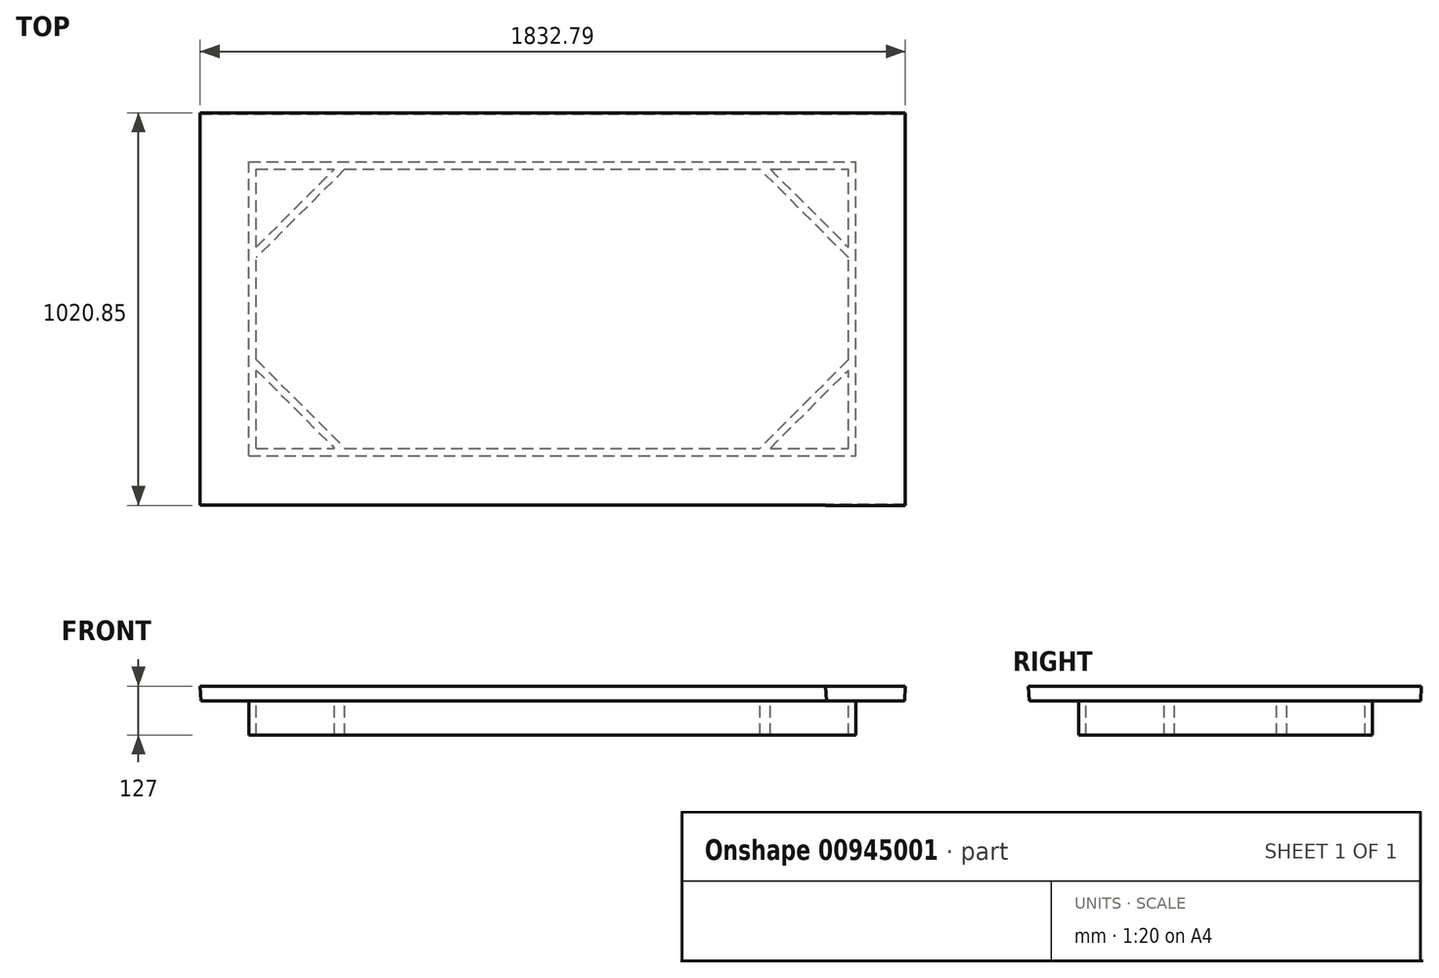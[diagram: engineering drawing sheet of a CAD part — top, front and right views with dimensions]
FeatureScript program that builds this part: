
annotation { "Feature Type Name" : "Feature", "Feature Type Description" : "" }
export const myFeature = defineFeature(function(context is Context, id is Id, definition is map)
    precondition{}
    {
        {
            var Q0;
            Q0=qCreatedBy(makeId("Top.planeOp"),FACE);
            var sketch = newSketch(context, id + "F0", { "sketchPlane" : qUnion([Q0])});
            skLineSegment(sketch, "E0.bottom", {"start": v(-617.33, 1070.93) * mm, "end": v(805.07, 1070.93) * mm});
            skLineSegment(sketch, "E0.top", {"start": v(-617.33, 867.73) * mm, "end": v(805.07, 867.73) * mm});
            skLineSegment(sketch, "E0.left", {"start": v(-617.33, 1070.93) * mm, "end": v(-617.33, 867.73) * mm});
            skLineSegment(sketch, "E0.right", {"start": v(805.07, 1070.93) * mm, "end": v(805.07, 867.73) * mm});
            skLineSegment(sketch, "E1.top", {"start": v(-617.33, 664.53) * mm, "end": v(805.07, 664.53) * mm});
            skLineSegment(sketch, "E1.left", {"start": v(-617.33, 867.73) * mm, "end": v(-617.33, 664.53) * mm});
            skLineSegment(sketch, "E1.right", {"start": v(805.07, 867.73) * mm, "end": v(805.07, 664.53) * mm});
            skLineSegment(sketch, "E2.top", {"start": v(-617.33, 461.33) * mm, "end": v(805.07, 461.33) * mm});
            skLineSegment(sketch, "E2.left", {"start": v(-617.33, 664.53) * mm, "end": v(-617.33, 461.33) * mm});
            skLineSegment(sketch, "E2.right", {"start": v(805.07, 664.53) * mm, "end": v(805.07, 461.33) * mm});
            skLineSegment(sketch, "E3.top", {"start": v(-617.33, 1274.13) * mm, "end": v(805.07, 1274.13) * mm});
            skLineSegment(sketch, "E3.left", {"start": v(-617.33, 1070.93) * mm, "end": v(-617.33, 1274.13) * mm});
            skLineSegment(sketch, "E3.right", {"start": v(805.07, 1070.93) * mm, "end": v(805.07, 1274.13) * mm});
            skLineSegment(sketch, "E4.top", {"start": v(-617.33, 258.13) * mm, "end": v(805.07, 258.13) * mm});
            skLineSegment(sketch, "E4.left", {"start": v(-617.33, 461.33) * mm, "end": v(-617.33, 258.13) * mm});
            skLineSegment(sketch, "E4.right", {"start": v(805.07, 461.33) * mm, "end": v(805.07, 258.13) * mm});
            skLineSegment(sketch, "E5.bottom", {"start": v(805.07, 1274.13) * mm, "end": v(1008.27, 1274.13) * mm});
            skLineSegment(sketch, "E5.top", {"start": v(805.07, 257.27) * mm, "end": v(1008.27, 257.27) * mm});
            skLineSegment(sketch, "E5.left", {"start": v(805.07, 1274.13) * mm, "end": v(805.07, 257.27) * mm});
            skLineSegment(sketch, "E5.right", {"start": v(1008.27, 1274.13) * mm, "end": v(1008.27, 257.27) * mm});
            skLineSegment(sketch, "E6.bottom", {"start": v(-617.33, 1274.13) * mm, "end": v(-820.53, 1274.13) * mm});
            skLineSegment(sketch, "E6.top", {"start": v(-617.33, 258.13) * mm, "end": v(-820.53, 258.13) * mm});
            skLineSegment(sketch, "E6.left", {"start": v(-617.33, 1274.13) * mm, "end": v(-617.33, 258.13) * mm});
            skLineSegment(sketch, "E6.right", {"start": v(-820.53, 1274.13) * mm, "end": v(-820.53, 258.13) * mm});
            skSolve(sketch);
        }
        {
            var Q0;
            {Q0=qUnion([makeQuery(id+"F0.imprint","IMPRINT",FACE,{"disambiguationData":[TD([[makeQuery(id+"F0.imprint","IMPRINT",EDGE,{"derivedFrom":sQuery(id+"F0.wireOp",EDGE,"E0.right")}),1.0]])]}),makeQuery(id+"F0.imprint","IMPRINT",FACE,{"disambiguationData":[TD([[makeQuery(id+"F0.imprint","IMPRINT",EDGE,{"derivedFrom":sQuery(id+"F0.wireOp",EDGE,"E0.bottom")}),1.0]])]}),makeQuery(id+"F0.imprint","IMPRINT",FACE,{"disambiguationData":[TD([[makeQuery(id+"F0.imprint","IMPRINT",EDGE,{"derivedFrom":sQuery(id+"F0.wireOp",EDGE,"E2.top")}),-1.0]])]}),makeQuery(id+"F0.imprint","IMPRINT",FACE,{"disambiguationData":[TD([[makeQuery(id+"F0.imprint","IMPRINT",EDGE,{"derivedFrom":sQuery(id+"F0.wireOp",EDGE,"E0.left")}),-1.0]])]})]);}
            var Q1;
            Q1=makeQuery(id+"F0.imprint","IMPRINT",FACE,{"disambiguationData":[TD([[makeQuery(id+"F0.imprint","IMPRINT",EDGE,{"derivedFrom":sQuery(id+"F0.wireOp",EDGE,"E0.bottom")}),-1.0]])]});
            var Q2;
            Q2=makeQuery(id+"F0.imprint","IMPRINT",FACE,{"disambiguationData":[TD([[makeQuery(id+"F0.imprint","IMPRINT",EDGE,{"derivedFrom":sQuery(id+"F0.wireOp",EDGE,"E0.top")}),-1.0]])]});
            var Q3;
            Q3=makeQuery(id+"F0.imprint","IMPRINT",FACE,{"disambiguationData":[TD([[makeQuery(id+"F0.imprint","IMPRINT",EDGE,{"derivedFrom":sQuery(id+"F0.wireOp",EDGE,"E1.top")}),-1.0]])]});
            extrude(context, id + "F1", {"entities" : qUnion([Q0, Q1, Q2, Q3]), "depth" : 38.1 * mm, "offsetDistance" : 25.4 * mm, "hasDraft" : true, "draftAngle" : 3 * degree});
        }
        {
            var Q0;
            Q0=makeQuery(id+"F1.opExtrude","CAP_FACE",FACE,{"disambiguationData":[OSD([sQuery(id+"F0.wireOp",EDGE,"E3.top"),sQuery(id+"F0.wireOp",EDGE,"E4.top"),sQuery(id+"F0.wireOp",EDGE,"E5.bottom"),sQuery(id+"F0.wireOp",EDGE,"E5.top"),sQuery(id+"F0.wireOp",EDGE,"E5.left"),sQuery(id+"F0.wireOp",EDGE,"E5.right"),sQuery(id+"F0.wireOp",EDGE,"E6.bottom"),sQuery(id+"F0.wireOp",EDGE,"E6.top"),sQuery(id+"F0.wireOp",EDGE,"E6.right")])],"isStart":true});
            var sketch = newSketch(context, id + "F2", { "sketchPlane" : qUnion([Q0])});
            skLineSegment(sketch, "E7.bottom", {"start": v(-695.53, -385.13) * mm, "end": v(881.27, -385.13) * mm});
            skLineSegment(sketch, "E7.top", {"start": v(-695.53, -1149.12) * mm, "end": v(881.27, -1149.12) * mm});
            skLineSegment(sketch, "E7.left", {"start": v(-695.53, -385.13) * mm, "end": v(-695.53, -1149.12) * mm});
            skLineSegment(sketch, "E7.right", {"start": v(881.27, -385.13) * mm, "end": v(881.27, -1149.12) * mm});
            skLineSegment(sketch, "E8.bottom", {"start": v(-676.48, -404.18) * mm, "end": v(862.22, -404.18) * mm});
            skLineSegment(sketch, "E8.top", {"start": v(-676.48, -1130.07) * mm, "end": v(862.22, -1130.07) * mm});
            skLineSegment(sketch, "E8.left", {"start": v(-676.48, -404.18) * mm, "end": v(-676.48, -1130.07) * mm});
            skLineSegment(sketch, "E8.right", {"start": v(862.22, -404.18) * mm, "end": v(862.22, -1130.07) * mm});
            skLineSegment(sketch, "E9", {"start": v(-676.48, -607.38) * mm, "end": v(-473.28, -404.18) * mm});
            skLineSegment(sketch, "E10", {"start": v(-676.48, -926.87) * mm, "end": v(-473.28, -1130.07) * mm});
            skLineSegment(sketch, "E11", {"start": v(-473.28, -1130.07) * mm, "end": v(-446.34, -1130.07) * mm});
            skLineSegment(sketch, "E12", {"start": v(-446.34, -1130.07) * mm, "end": v(-676.48, -899.93) * mm});
            skLineSegment(sketch, "E13", {"start": v(-676.48, -899.93) * mm, "end": v(-676.48, -926.87) * mm});
            skLineSegment(sketch, "E14", {"start": v(-676.48, -607.38) * mm, "end": v(-676.48, -634.32) * mm});
            skLineSegment(sketch, "E15", {"start": v(-676.48, -634.32) * mm, "end": v(-446.34, -404.18) * mm});
            skLineSegment(sketch, "E16", {"start": v(-446.34, -404.18) * mm, "end": v(-473.28, -404.18) * mm});
            skLineSegment(sketch, "E17", {"start": v(659.02, -404.18) * mm, "end": v(862.22, -607.38) * mm});
            skLineSegment(sketch, "E18", {"start": v(862.22, -607.38) * mm, "end": v(862.22, -634.32) * mm});
            skLineSegment(sketch, "E19", {"start": v(862.22, -634.32) * mm, "end": v(632.08, -404.18) * mm});
            skLineSegment(sketch, "E20", {"start": v(632.08, -404.18) * mm, "end": v(659.02, -404.18) * mm});
            skLineSegment(sketch, "E21", {"start": v(862.22, -926.87) * mm, "end": v(862.22, -899.93) * mm});
            skLineSegment(sketch, "E22", {"start": v(862.22, -899.93) * mm, "end": v(632.08, -1130.07) * mm});
            skLineSegment(sketch, "E23", {"start": v(632.08, -1130.07) * mm, "end": v(659.02, -1130.07) * mm});
            skLineSegment(sketch, "E24", {"start": v(659.02, -1130.07) * mm, "end": v(862.22, -926.87) * mm});
            skLineSegment(sketch, "E25.bottom", {"start": v(-676.48, -404.18) * mm, "end": v(-574.88, -404.18) * mm});
            skLineSegment(sketch, "E25.top", {"start": v(-676.48, -505.78) * mm, "end": v(-574.88, -505.78) * mm});
            skLineSegment(sketch, "E25.left", {"start": v(-676.48, -404.18) * mm, "end": v(-676.48, -505.78) * mm});
            skLineSegment(sketch, "E25.right", {"start": v(-574.88, -404.18) * mm, "end": v(-574.88, -505.78) * mm});
            skSolve(sketch);
        }
        {
            var Q0;
            Q0=makeQuery(id+"F2.imprint","IMPRINT",FACE,{"disambiguationData":[TD([[makeQuery(id+"F2.imprint","IMPRINT",EDGE,{"derivedFrom":sQuery(id+"F2.wireOp",EDGE,"E7.bottom")}),-1.0]])]});
            var Q1;
            {var subQ6=sQuery(id+"F2.wireOp",EDGE,"E15");Q1=makeQuery(id+"F2.imprint","IMPRINT",FACE,{"disambiguationData":[TD([[makeQuery(id+"F2.imprint","IMPRINT",EDGE,{"derivedFrom":subQ6}),1.0]])]});}
            var Q2;
            {var subQ2=sQuery(id+"F2.wireOp",EDGE,"E10");Q2=makeQuery(id+"F2.imprint","IMPRINT",FACE,{"disambiguationData":[TD([[makeQuery(id+"F2.imprint","IMPRINT",EDGE,{"derivedFrom":subQ2}),1.0]])]});}
            var Q3;
            {var subQ0=sQuery(id+"F2.wireOp",EDGE,"E22");Q3=makeQuery(id+"F2.imprint","IMPRINT",FACE,{"disambiguationData":[TD([[makeQuery(id+"F2.imprint","IMPRINT",EDGE,{"derivedFrom":subQ0}),1.0]])]});}
            var Q4;
            {var subQ0=sQuery(id+"F2.wireOp",EDGE,"E17");Q4=makeQuery(id+"F2.imprint","IMPRINT",FACE,{"disambiguationData":[TD([[makeQuery(id+"F2.imprint","IMPRINT",EDGE,{"derivedFrom":subQ0}),-1.0]])]});}
            extrude(context, id + "F3", {"entities" : qUnion([Q0, Q1, Q2, Q3, Q4]), "operationType" : NewBodyOperationType.ADD, "depth" : 88.9 * mm, "offsetDistance" : 25.4 * mm});
        }
    });
